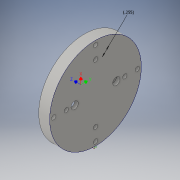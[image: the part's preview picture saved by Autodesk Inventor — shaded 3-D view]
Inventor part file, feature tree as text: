
AUTODESK INVENTOR PART (.ipt)
format: ipt  version: 2016 (Build 200138000, 138)  size: 308,224 bytes
history: native  units: in
note: dims shown in document units (in); Inventor stores cm internally (conversion verified against a paired STEP export)
features: sketch x6, extrude x3, revolve x1
ambient origin geometry x8: Origin, YZ Plane, XZ Plane, XY Plane, X Axis, Y Axis, Z Axis, Center Point
bodies: Solid1 (feature_tree)
feature tree (10):
  revolve  "Revolution1"  [1 undecoded]
  extrude  "Extrusion1"  Depth=0.105in
  sketch  "Sketch3"  dims[d4=0.105in d5=0.255in]
  sketch  "Sketch4"  dims[d6=0.2in d7=0.1in]
  extrude  "Extrusion2"  Depth=0.105in
  sketch  "Sketch5"  dims[d8=90.0deg]
  extrude  "Extrusion4"  Depth=0.1in
  sketch  "Sketch1"  dims[d0=1.2499in d1=0.3in]
  sketch  "Sketch2"  dims[d2=0.22in d3=0.105in]
  sketch  "Sketch8"  dims[d9=0.1181in d10=1.5748in d12=360.0deg d14=0.5in d15=0.0in d16=0.255in d17=0.1275in d18=0.1181in d19=1.5748in d21=360.0deg d23=0.2in d24=0.0in d25=1.14in d26=0.787in d42=1.0in d43=0.0in]
note: 1 required parameter value undecoded (feature->parameter linkage not recoverable at this tier; creation-order binding heuristic only, values carry confidence <= 0.55)
